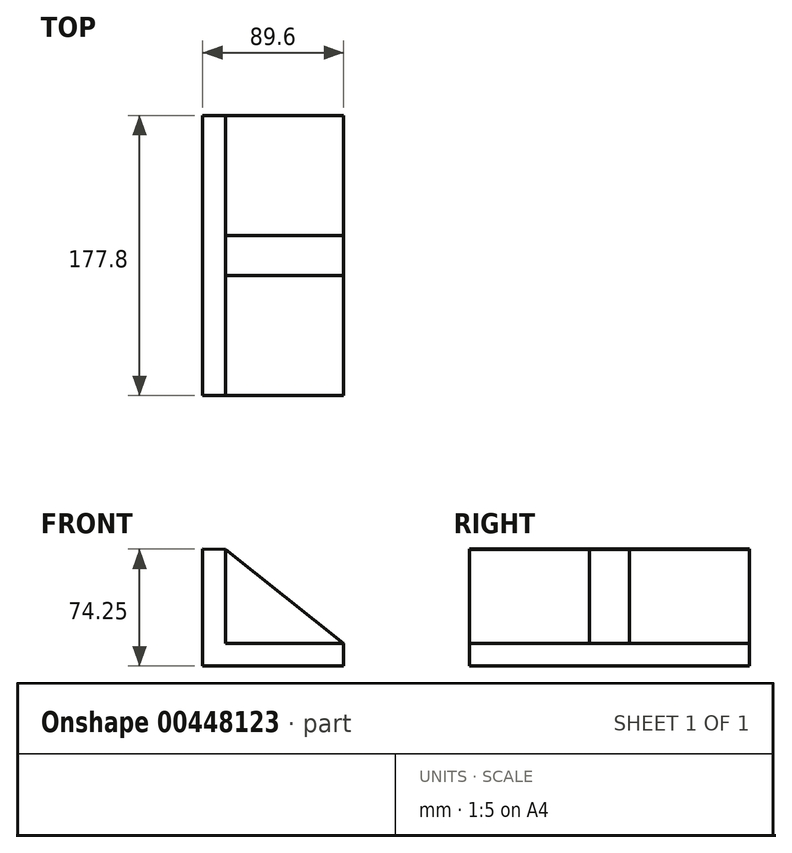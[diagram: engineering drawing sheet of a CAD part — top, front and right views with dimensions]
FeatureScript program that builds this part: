
annotation { "Feature Type Name" : "Feature", "Feature Type Description" : "" }
export const myFeature = defineFeature(function(context is Context, id is Id, definition is map)
    precondition{}
    {
        {
            var Q0;
            Q0=qCreatedBy(makeId("Front.planeOp"),FACE);
            var sketch = newSketch(context, id + "F0", { "sketchPlane" : qUnion([Q0])});
            skLineSegment(sketch, "E0", {"start": v(-41.6, 37.4) * mm, "end": v(-41.6, -36.85) * mm});
            skLineSegment(sketch, "E1", {"start": v(-41.6, -36.85) * mm, "end": v(48.01, -36.85) * mm});
            skLineSegment(sketch, "E2", {"start": v(48.01, -36.85) * mm, "end": v(48.01, -22.61) * mm});
            skLineSegment(sketch, "E3", {"start": v(48.01, -22.61) * mm, "end": v(-27.08, -22.61) * mm});
            skLineSegment(sketch, "E4", {"start": v(-27.08, -22.61) * mm, "end": v(-27.08, 37.12) * mm});
            skLineSegment(sketch, "E5", {"start": v(-27.08, 37.12) * mm, "end": v(-41.6, 37.4) * mm});
            skLineSegment(sketch, "E6", {"start": v(-27.08, 37.12) * mm, "end": v(48.01, -22.61) * mm});
            skSolve(sketch);
        }
        {
            var Q0;
            Q0=makeQuery(id+"F0.imprint","IMPRINT",FACE,{"disambiguationData":[TD([[makeQuery(id+"F0.imprint","IMPRINT",EDGE,{"derivedFrom":sQuery(id+"F0.wireOp",EDGE,"E0")}),1.0]])]});
            extrude(context, id + "F1", {"entities" : qUnion([Q0]), "endBound" : BoundingType.SYMMETRIC, "depth" : 177.8 * mm});
        }
        {
            var Q0;
            Q0 = qSketchRegion(id + "F0", true);
            extrude(context, id + "F2", {"entities" : qUnion([Q0]), "operationType" : NewBodyOperationType.ADD, "endBound" : BoundingType.SYMMETRIC, "depth" : 25.4 * mm});
        }
    });
